# Revit family: QF_Cool-Compact_Abfallkuehler_3x120L_ZK
name_source: partatom
category: Sonderausstattung
units: mm (PartAtom-declared; Revit-internal decimal feet)

## family parameters
Arbeitsebenenbasiert = Nein
Beim Laden mit Abzugskörper schneiden = Nein
Bemaßung runder Anschluss = Durchmesser verwenden
Gemeinsam genutzt = Nein
Immer vertikal = Ja
OmniClass-Nummer = 23.70.30.21.11
OmniClass-Titel = Complete Solid Waste Removal Systems
Raumberechnungspunkt = Nein
Teiletyp = Normal

## types (1)
- 1NAC / 230 V / 50 Hz
    Abwassertemperatur = 5 °C
    Anzahl der Pole = 1
    Beschreibung = Konfiskatkühler (3 x 120 Liter), zentralgekühlt
    CE Kennzeichnung = Ja
    Datenschnittstelle = Ja
    Datenschnittstelle Beschreibung = RS 485
    Frequenz = 50 Hz
    Gewicht = 185.00 kg
    Hersteller = Cool Compact
    Höhe = 1030 mm  [stored 3.37927 ft]
    Indirekte Ablaufanschlussgröße = 19 mm
    Indirekter Abwasserstrom = 0.0 L/s
    Kälte Abmessung Flüssigkeitsleitung = 6 mm
    Kälte Abmessung Saugleitung = 8 mm
    Kälte Klimaklasse = 5
    Kälte Tauwasserablauf = Ja
    Kälte Verdampfungstemperatur = -15 °C
    Kälteleistung = 322 W
    Länge Gerätebreite = 2400 mm  [stored 7.87402 ft]
    Modell = AKO031200
    Phasen = 1
    Spannung = 230 V
    Stecker System = Schuko / T13
    Tiefe = 720 mm  [stored 2.3622 ft]
    URL = https://www.coolcompact.de
    Vorgabe-Ansicht = 0 mm  [stored 0 ft]
    Watt Leistung = 120 W
    Zuleitung zum Gerät im Lieferumfang = Ja

note: [stored X ft] marks values corroborated as IEEE doubles in the binary element streams (Revit-internal decimal feet)
